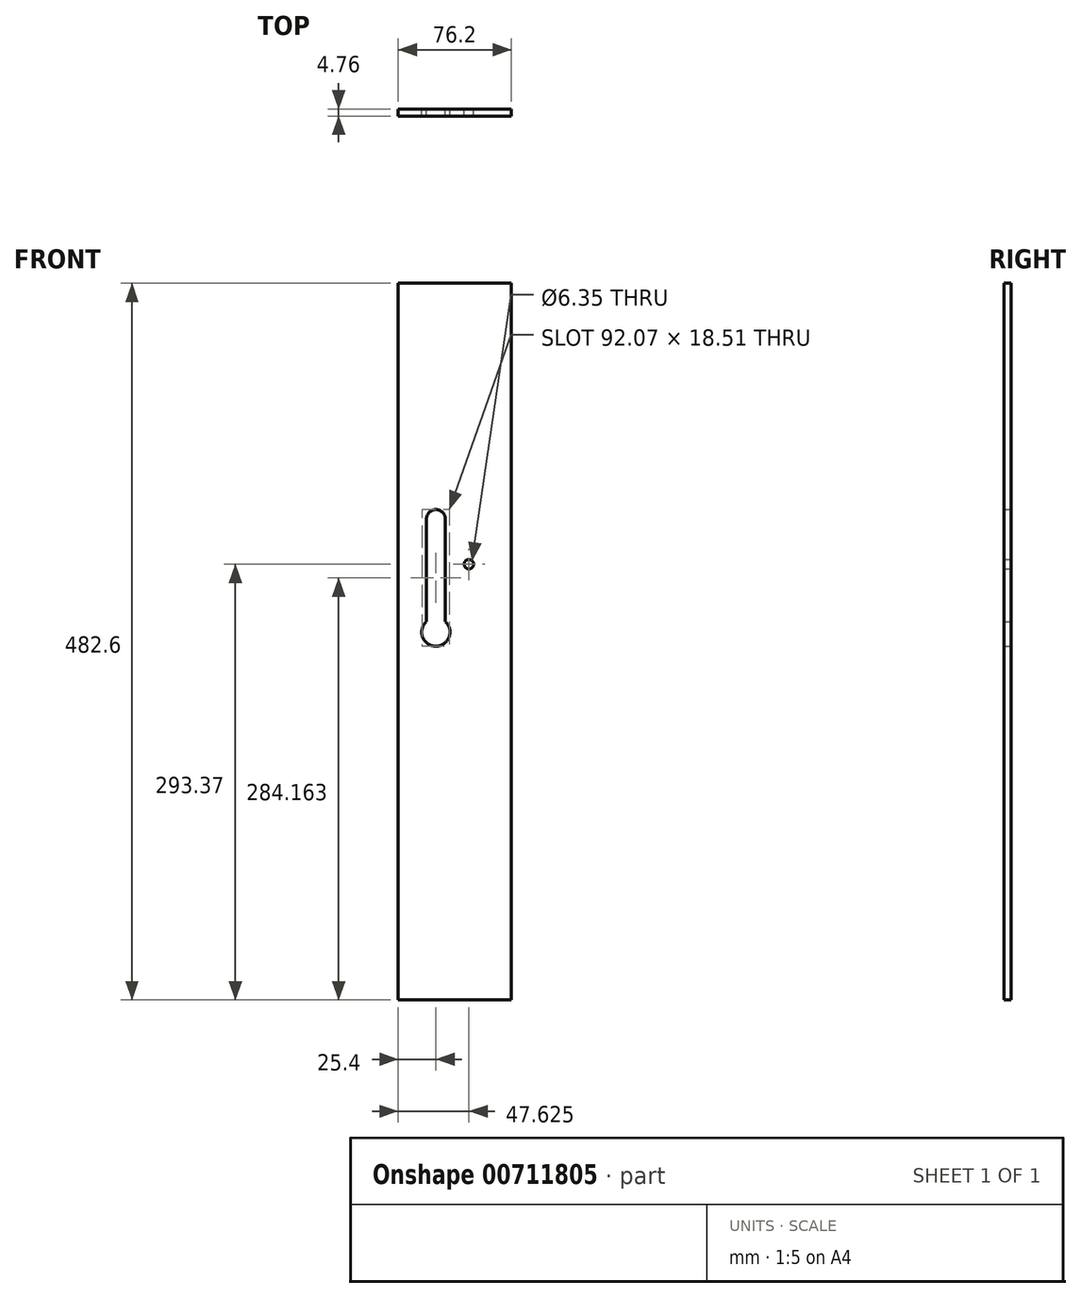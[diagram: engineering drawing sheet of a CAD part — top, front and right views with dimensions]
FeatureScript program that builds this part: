
annotation { "Feature Type Name" : "Feature", "Feature Type Description" : "" }
export const myFeature = defineFeature(function(context is Context, id is Id, definition is map)
    precondition{}
    {
        {
            var Q0;
            Q0=qCreatedBy(makeId("Front.planeOp"),FACE);
            var sketch = newSketch(context, id + "F0", { "sketchPlane" : qUnion([Q0])});
            skLineSegment(sketch, "E0.bottom", {"start": v(0, 0) * mm, "end": v(76.2, 0) * mm});
            skLineSegment(sketch, "E0.top", {"start": v(0, 482.6) * mm, "end": v(76.2, 482.6) * mm});
            skLineSegment(sketch, "E0.left", {"start": v(0, 0) * mm, "end": v(0, 482.6) * mm});
            skLineSegment(sketch, "E0.right", {"start": v(76.2, 0) * mm, "end": v(76.2, 482.6) * mm});
            skArc(sketch, "E1", {"start": v(19.05, 254.75) * mm, "mid": v(25.4, 238.13) * mm, "end": v(31.75, 254.75) * mm});
            skArc(sketch, "E2", {"start": v(31.75, 323.85) * mm, "mid": v(25.4, 330.2) * mm, "end": v(19.05, 323.85) * mm});
            skLineSegment(sketch, "E3", {"start": v(19.05, 323.85) * mm, "end": v(19.05, 254.75) * mm});
            skLineSegment(sketch, "E4", {"start": v(31.75, 323.85) * mm, "end": v(31.75, 254.75) * mm});
            skCircle(sketch, "E5", {"center": v(47.62, 293.37) * mm, "radius": 3.18 * mm});
            skSolve(sketch);
        }
        {
            var Q0;
            Q0=makeQuery(id+"F0.imprint","IMPRINT",FACE,{"disambiguationData":[TD([[makeQuery(id+"F0.imprint","IMPRINT",EDGE,{"derivedFrom":sQuery(id+"F0.wireOp",EDGE,"E0.bottom")}),1.0]])]});
            extrude(context, id + "F1", {"entities" : qUnion([Q0]), "depth" : 4.76 * mm, "offsetDistance" : 25.4 * mm});
        }
    });
